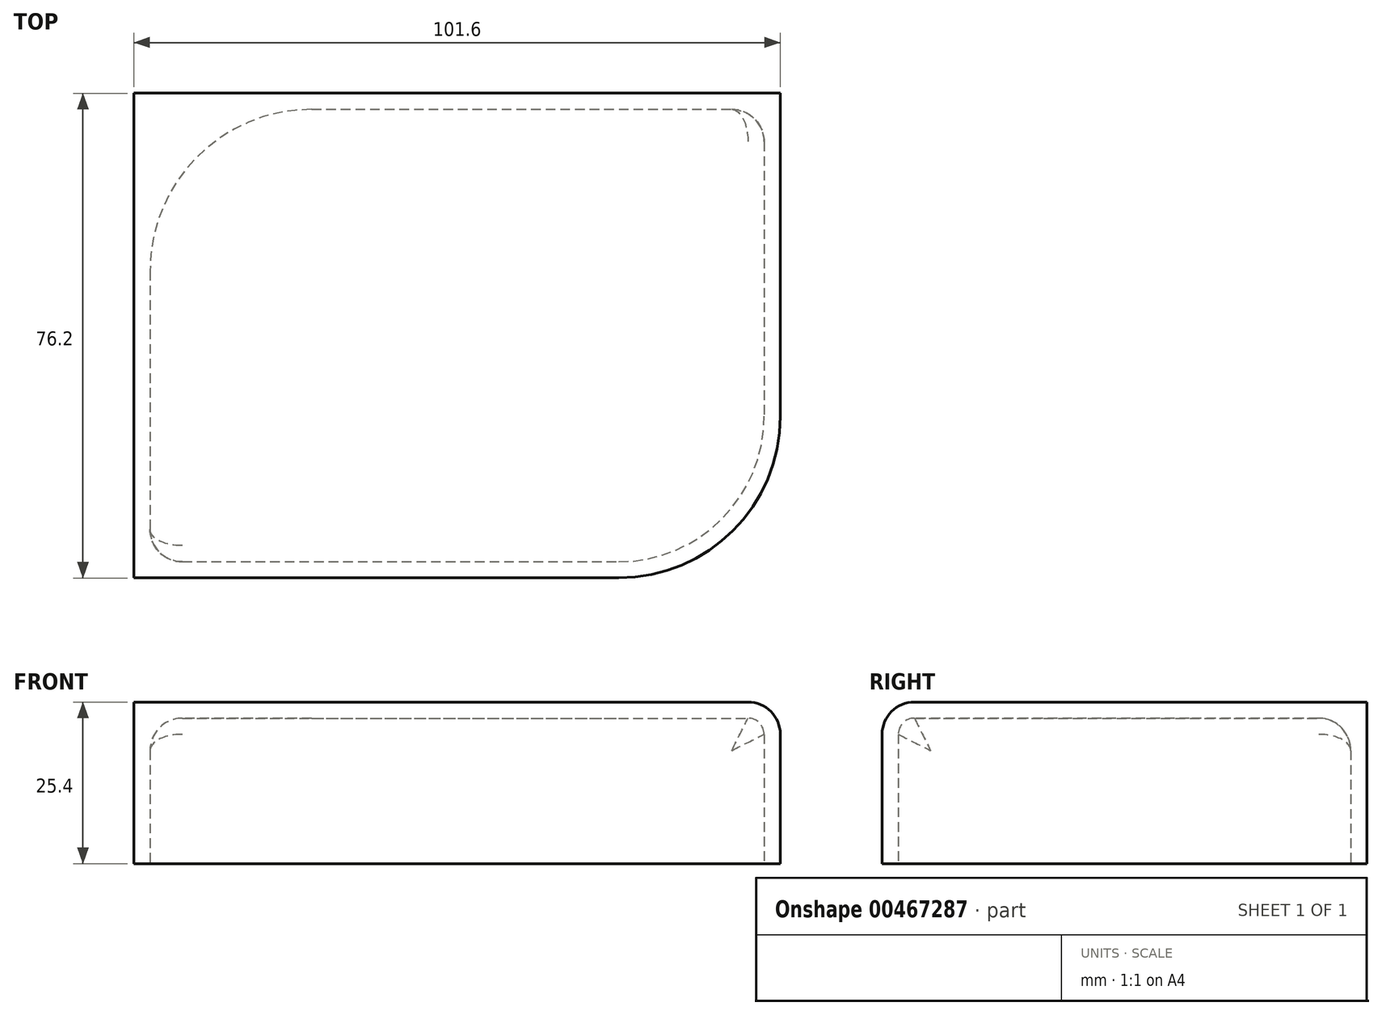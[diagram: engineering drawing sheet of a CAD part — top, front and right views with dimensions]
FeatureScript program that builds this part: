
annotation { "Feature Type Name" : "Feature", "Feature Type Description" : "" }
export const myFeature = defineFeature(function(context is Context, id is Id, definition is map)
    precondition{}
    {
        {
            var Q0;
            Q0=qCreatedBy(makeId("Top.planeOp"),FACE);
            var sketch = newSketch(context, id + "F0", { "sketchPlane" : qUnion([Q0])});
            skLineSegment(sketch, "E0.bottom", {"start": v(-53.18, 10.14) * mm, "end": v(48.42, 10.14) * mm});
            skLineSegment(sketch, "E0.top", {"start": v(-53.18, -66.06) * mm, "end": v(23.02, -66.06) * mm});
            skLineSegment(sketch, "E0.left", {"start": v(-53.18, 10.14) * mm, "end": v(-53.18, -66.06) * mm});
            skLineSegment(sketch, "E0.right", {"start": v(48.42, 10.14) * mm, "end": v(48.42, -40.66) * mm});
            skPoint(sketch, "E1.visualSharp", {"position": v(48.42, -66.06) * mm});
            skArc(sketch, "E1.filletArc", {"start": v(23.02, -66.06) * mm, "mid": v(40.98, -58.62) * mm, "end": v(48.42, -40.66) * mm});
            skSolve(sketch);
        }
        {
            var Q0;
            Q0 = qSketchRegion(id + "F0", true);
            extrude(context, id + "F1", {"entities" : qUnion([Q0]), "depth" : 25.4 * mm});
        }
        {
            var Q0;
            Q0=makeQuery(id+"F1.opExtrude","CAP_EDGE",EDGE,{"disambiguationData":[OSD([sQuery(id+"F0.wireOp",EDGE,"E0.top")])],"isStart":false});
            fillet(context, id + "F2", {"entities" : qUnion([Q0]), "radius" : 5.08 * mm, "tangentPropagation" : true, "allowEdgeOverflow" : false});
        }
        {
            var Q0;
            Q0=makeQuery(id+"F1.opExtrude","CAP_FACE",FACE,{"disambiguationData":[OSD([sQuery(id+"F0.wireOp",EDGE,"E0.bottom"),sQuery(id+"F0.wireOp",EDGE,"E0.top"),sQuery(id+"F0.wireOp",EDGE,"E0.left"),sQuery(id+"F0.wireOp",EDGE,"E0.right"),sQuery(id+"F0.wireOp",EDGE,"E1.filletArc")])],"isStart":true});
            var Q1;
            Q1=makeQuery(id+"F1.opExtrude","SWEPT_BODY",BODY,{"disambiguationData":[OSD([sQuery(id+"F0.wireOp",EDGE,"E0.bottom"),sQuery(id+"F0.wireOp",EDGE,"E0.top"),sQuery(id+"F0.wireOp",EDGE,"E0.left"),sQuery(id+"F0.wireOp",EDGE,"E0.right"),sQuery(id+"F0.wireOp",EDGE,"E1.filletArc")])]});
            shell(context, id + "F3", {"entities" : qUnion([Q0]), "parts" : qUnion([Q1]), "thickness" : 2.54 * mm});
        }
        {
            var Q0;
            Q0=makeQuery(id+"F3.opShell","OFFSET_EDGE",EDGE,{"disambiguationData":[OSD([sQuery(id+"F0.wireOp",EDGE,"E0.bottom"),sQuery(id+"F0.wireOp",EDGE,"E0.left")])]});
            fillet(context, id + "F4", {"entities" : qUnion([Q0]), "radius" : 25.4 * mm, "tangentPropagation" : true, "allowEdgeOverflow" : false});
        }
        {
            var Q0;
            {var subQ0=sQuery(id+"F0.wireOp",EDGE,"E0.left");Q0=makeQuery(id+"F3.opShell","OFFSET_EDGE",EDGE,{"disambiguationData":[OSD([subQ0]),TDD([makeQuery(id+"F1.opExtrude","CAP_EDGE",EDGE,{"disambiguationData":[OSD([subQ0])],"isStart":false})])]});}
            fillet(context, id + "F5", {"entities" : qUnion([Q0]), "radius" : 5.08 * mm, "tangentPropagation" : true, "allowEdgeOverflow" : false});
        }
    });
